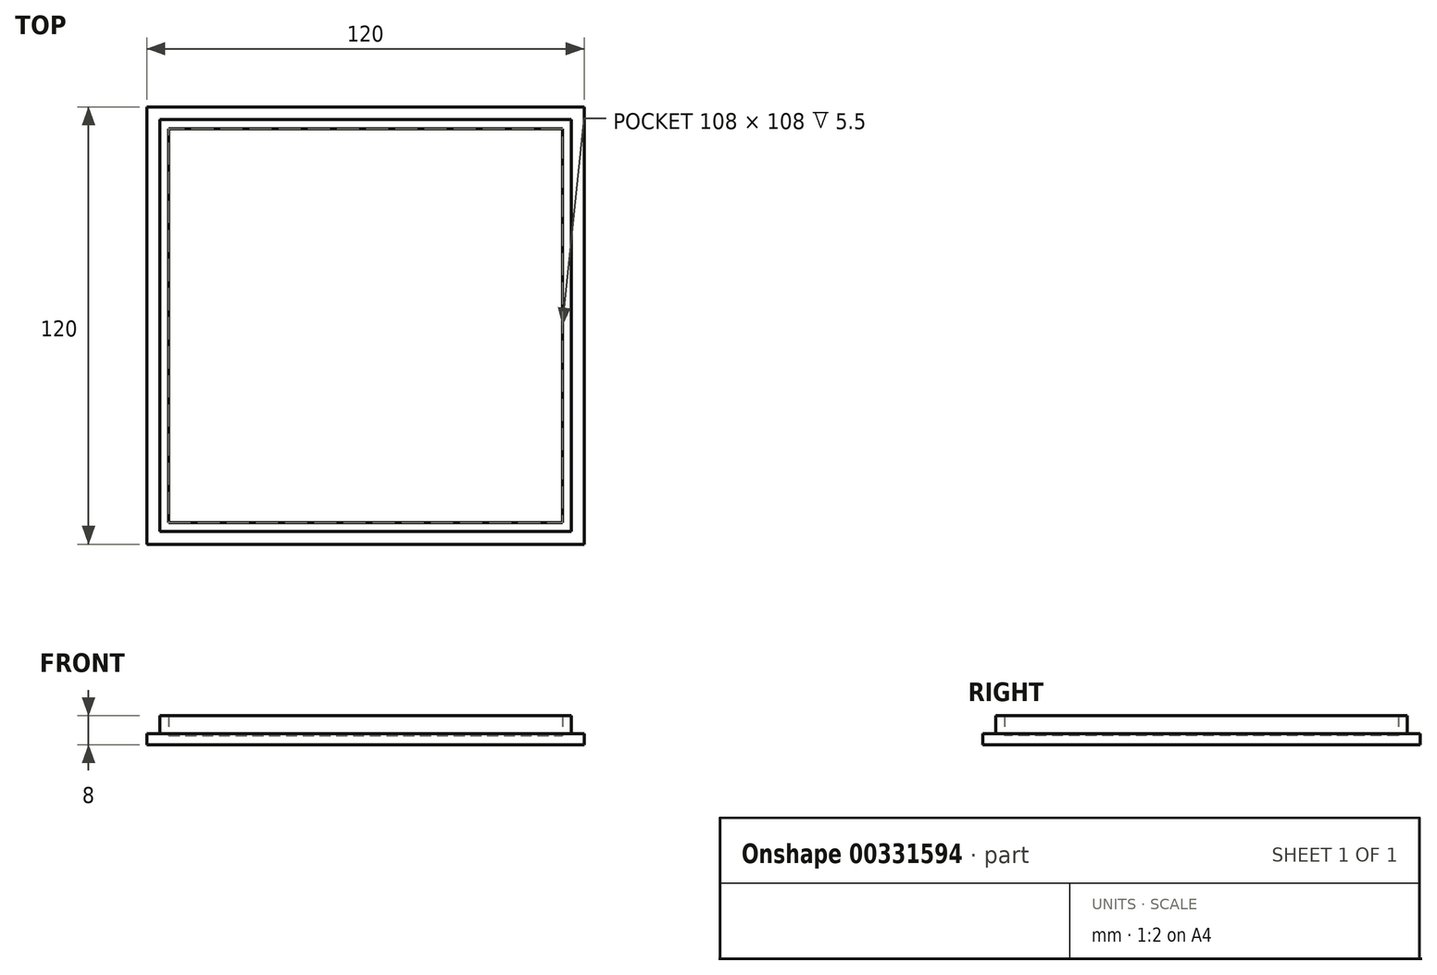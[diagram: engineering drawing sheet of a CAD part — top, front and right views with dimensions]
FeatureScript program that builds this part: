
annotation { "Feature Type Name" : "Feature", "Feature Type Description" : "" }
export const myFeature = defineFeature(function(context is Context, id is Id, definition is map)
    precondition{}
    {
        {
            var Q0;
            Q0=qCreatedBy(makeId("Top.planeOp"),FACE);
            var sketch = newSketch(context, id + "F0", { "sketchPlane" : qUnion([Q0])});
            skLineSegment(sketch, "E0.bottom", {"start": v(60, -60) * mm, "end": v(-60, -60) * mm});
            skLineSegment(sketch, "E0.top", {"start": v(60, 60) * mm, "end": v(-60, 60) * mm});
            skLineSegment(sketch, "E0.left", {"start": v(60, -60) * mm, "end": v(60, 60) * mm});
            skLineSegment(sketch, "E0.right", {"start": v(-60, -60) * mm, "end": v(-60, 60) * mm});
            skPoint(sketch, "E0.middle", {"position": v(0, 0) * mm});
            skSolve(sketch);
        }
        {
            var Q0;
            Q0=qSketchRegion(id+"F0",true);
            extrude(context, id + "F1", {"entities" : qUnion([Q0]), "depth" : 3 * mm});
        }
        {
            var Q0;
            Q0=makeQuery(id+"F1.opExtrude","CAP_FACE",FACE,{"disambiguationData":[OSD([sQuery(id+"F0.wireOp",EDGE,"E0.bottom"),sQuery(id+"F0.wireOp",EDGE,"E0.top"),sQuery(id+"F0.wireOp",EDGE,"E0.left"),sQuery(id+"F0.wireOp",EDGE,"E0.right")])],"isStart":false});
            var sketch = newSketch(context, id + "F2", { "sketchPlane" : qUnion([Q0])});
            skLineSegment(sketch, "E1.bottom", {"start": v(56.5, -56.5) * mm, "end": v(-56.5, -56.5) * mm});
            skLineSegment(sketch, "E1.top", {"start": v(56.5, 56.5) * mm, "end": v(-56.5, 56.5) * mm});
            skLineSegment(sketch, "E1.left", {"start": v(56.5, -56.5) * mm, "end": v(56.5, 56.5) * mm});
            skLineSegment(sketch, "E1.right", {"start": v(-56.5, -56.5) * mm, "end": v(-56.5, 56.5) * mm});
            skPoint(sketch, "E1.middle", {"position": v(0, 0) * mm});
            skSolve(sketch);
        }
        {
            var Q0;
            Q0=qSketchRegion(id+"F2",true);
            extrude(context, id + "F3", {"entities" : qUnion([Q0]), "operationType" : NewBodyOperationType.ADD, "depth" : 5 * mm});
        }
        {
            var Q0;
            Q0=makeQuery(id+"F3.opExtrude","CAP_FACE",FACE,{"disambiguationData":[OSD([sQuery(id+"F2.wireOp",EDGE,"E1.bottom"),sQuery(id+"F2.wireOp",EDGE,"E1.top"),sQuery(id+"F2.wireOp",EDGE,"E1.left"),sQuery(id+"F2.wireOp",EDGE,"E1.right")])],"isStart":false});
            shell(context, id + "F4", {"entities" : qUnion([Q0]), "thickness" : 2.5 * mm});
        }
    });
